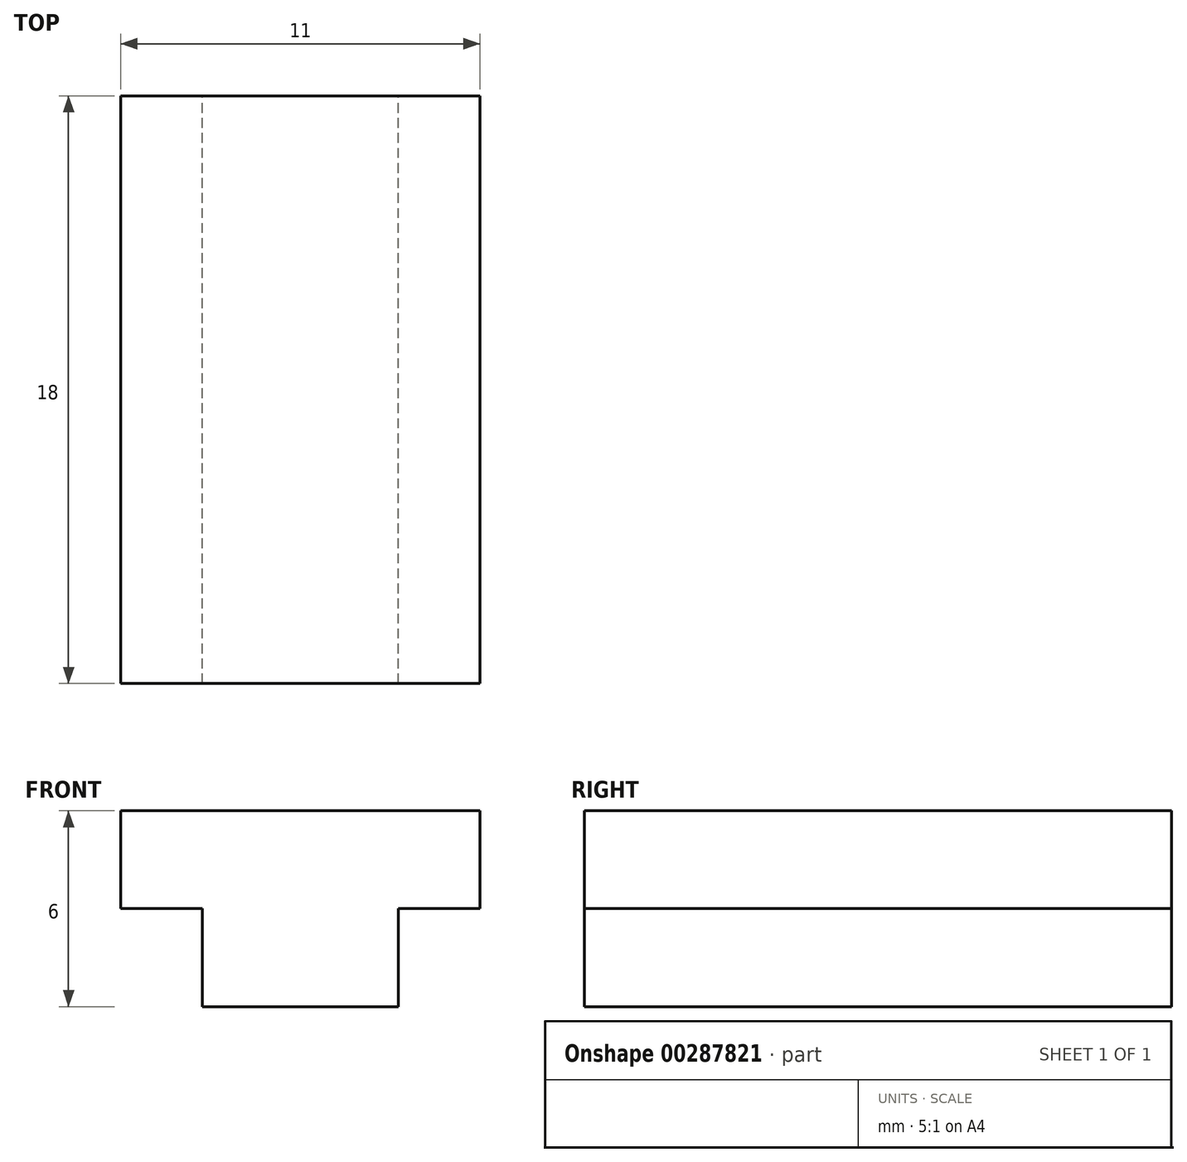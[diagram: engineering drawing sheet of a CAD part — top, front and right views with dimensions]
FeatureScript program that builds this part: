
annotation { "Feature Type Name" : "Feature", "Feature Type Description" : "" }
export const myFeature = defineFeature(function(context is Context, id is Id, definition is map)
    precondition{}
    {
        {
            var Q0;
            Q0=qCreatedBy(makeId("Front.planeOp"),FACE);
            var sketch = newSketch(context, id + "F0", { "sketchPlane" : qUnion([Q0])});
            skLineSegment(sketch, "E0", {"start": v(-8.5, 40.65) * mm, "end": v(2.5, 40.65) * mm});
            skLineSegment(sketch, "E1", {"start": v(2.5, 40.65) * mm, "end": v(2.5, 37.65) * mm});
            skLineSegment(sketch, "E2", {"start": v(-8.5, 40.65) * mm, "end": v(-8.5, 37.65) * mm});
            skLineSegment(sketch, "E3", {"start": v(2.5, 37.65) * mm, "end": v(0, 37.65) * mm});
            skLineSegment(sketch, "E4", {"start": v(0, 37.65) * mm, "end": v(0, 34.65) * mm});
            skLineSegment(sketch, "E5", {"start": v(-8.5, 37.65) * mm, "end": v(-6, 37.65) * mm});
            skLineSegment(sketch, "E6", {"start": v(-6, 37.65) * mm, "end": v(-6, 34.65) * mm});
            skLineSegment(sketch, "E7", {"start": v(-6, 34.65) * mm, "end": v(0, 34.65) * mm});
            skSolve(sketch);
        }
        {
            var Q0;
            Q0 = qSketchRegion(id + "F0", true);
            extrude(context, id + "F1", {"entities" : qUnion([Q0]), "depth" : 18 * mm});
        }
    });
